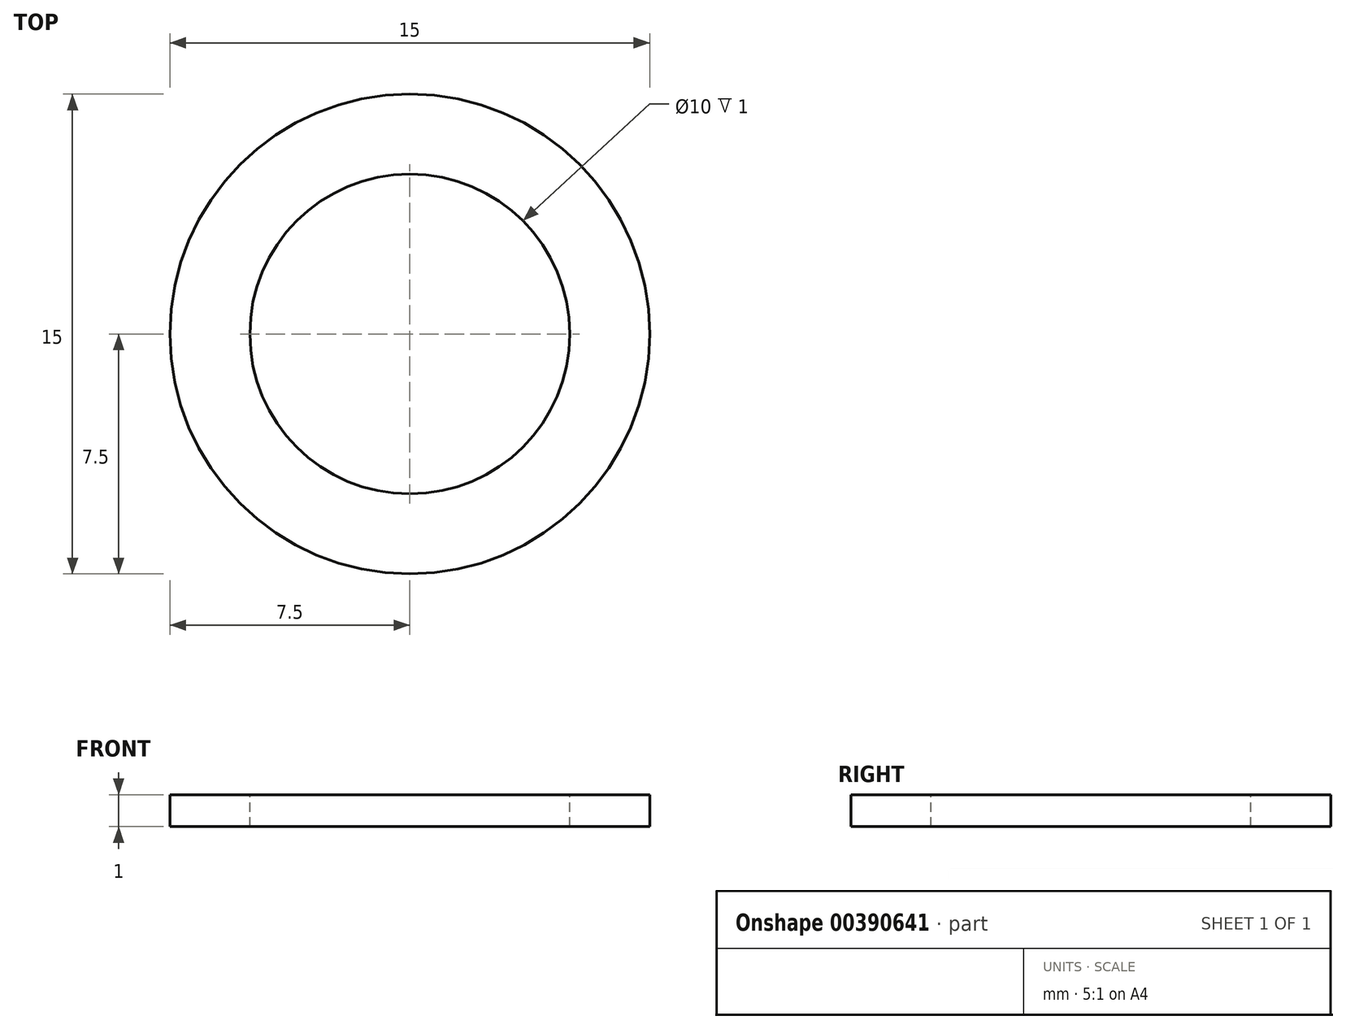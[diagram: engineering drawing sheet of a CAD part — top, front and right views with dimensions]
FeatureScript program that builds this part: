
annotation { "Feature Type Name" : "Feature", "Feature Type Description" : "" }
export const myFeature = defineFeature(function(context is Context, id is Id, definition is map)
    precondition{}
    {
        {
            var Q0;
            Q0=qCreatedBy(makeId("Top.planeOp"),FACE);
            var sketch = newSketch(context, id + "F0", { "sketchPlane" : qUnion([Q0])});
            skCircle(sketch, "E0", {"center": v(0, 0) * mm, "radius": 7.5 * mm});
            skSolve(sketch);
        }
        {
            var Q0;
            Q0 = qSketchRegion(id + "F0", true);
            extrude(context, id + "F1", {"entities" : qUnion([Q0]), "depth" : 1 * mm, "offsetDistance" : 25 * mm});
        }
        {
            var Q0;
            Q0=makeQuery(id+"F1.opExtrude","CAP_FACE",FACE,{"disambiguationData":[OSD([sQuery(id+"F0.wireOp",EDGE,"E0")])],"isStart":false});
            var sketch = newSketch(context, id + "F2", { "sketchPlane" : qUnion([Q0])});
            skCircle(sketch, "E1", {"center": v(0, 0) * mm, "radius": 5 * mm});
            skSolve(sketch);
        }
        {
            var Q0;
            Q0 = qSketchRegion(id + "F2", true);
            extrude(context, id + "F3", {"entities" : qUnion([Q0]), "operationType" : NewBodyOperationType.REMOVE, "endBound" : BoundingType.THROUGH_ALL, "oppositeDirection" : true, "depth" : 25 * mm});
        }
    });
